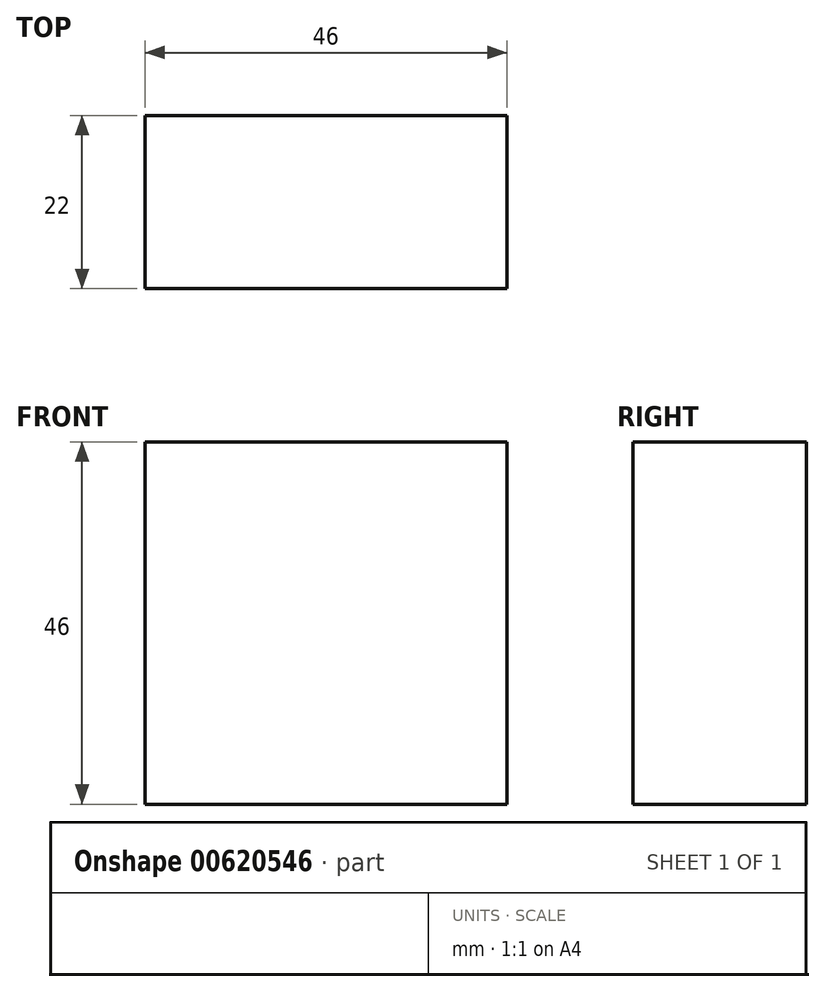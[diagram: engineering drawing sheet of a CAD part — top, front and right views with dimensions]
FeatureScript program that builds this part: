
annotation { "Feature Type Name" : "Feature", "Feature Type Description" : "" }
export const myFeature = defineFeature(function(context is Context, id is Id, definition is map)
    precondition{}
    {
        {
            var Q0;
            Q0=qCreatedBy(makeId("Front.planeOp"),FACE);
            var sketch = newSketch(context, id + "F0", { "sketchPlane" : qUnion([Q0])});
            skLineSegment(sketch, "E0.bottom", {"start": v(-23, -23) * mm, "end": v(23, -23) * mm});
            skLineSegment(sketch, "E0.top", {"start": v(-23, 23) * mm, "end": v(23, 23) * mm});
            skLineSegment(sketch, "E0.left", {"start": v(-23, -23) * mm, "end": v(-23, 23) * mm});
            skLineSegment(sketch, "E0.right", {"start": v(23, -23) * mm, "end": v(23, 23) * mm});
            skPoint(sketch, "E0.middle", {"position": v(0, 0) * mm});
            skSolve(sketch);
        }
        {
            var Q0;
            Q0=makeQuery(id+"F0.imprint","IMPRINT",FACE,{"disambiguationData":[TD([[makeQuery(id+"F0.imprint","IMPRINT",EDGE,{"derivedFrom":sQuery(id+"F0.wireOp",EDGE,"E0.bottom")}),1.0]])]});
            extrude(context, id + "F1", {"entities" : qUnion([Q0]), "depth" : 22 * mm, "offsetDistance" : 25 * mm});
        }
    });
